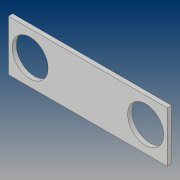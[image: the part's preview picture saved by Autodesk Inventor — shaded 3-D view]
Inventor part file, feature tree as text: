
AUTODESK INVENTOR PART (.ipt)
format: ipt  version: 2021 (Build 250183000, 183)  size: 107,008 bytes
history: native  units: mm
features: extrude x2, sketch x2
ambient origin geometry x8: Origin, YZ Plane, XZ Plane, XY Plane, X Axis, Y Axis, Z Axis, Center Point
bodies: Solid1 (feature_tree)
feature tree (4):
  extrude  "Extrusion1"  Depth=35.0mm
  extrude  "Extrusion2"  Depth=35.0mm
  sketch  "Sketch1"  dims[d0=35.0mm d1=55.0mm]
  sketch  "Sketch2"  dims[d2=110.0mm d3=35.0mm d4=3.0mm d5=0.0mm d6=25.0mm d7=40.0mm d8=25.0mm d9=40.0mm d10=5.0mm d11=0.0mm]
